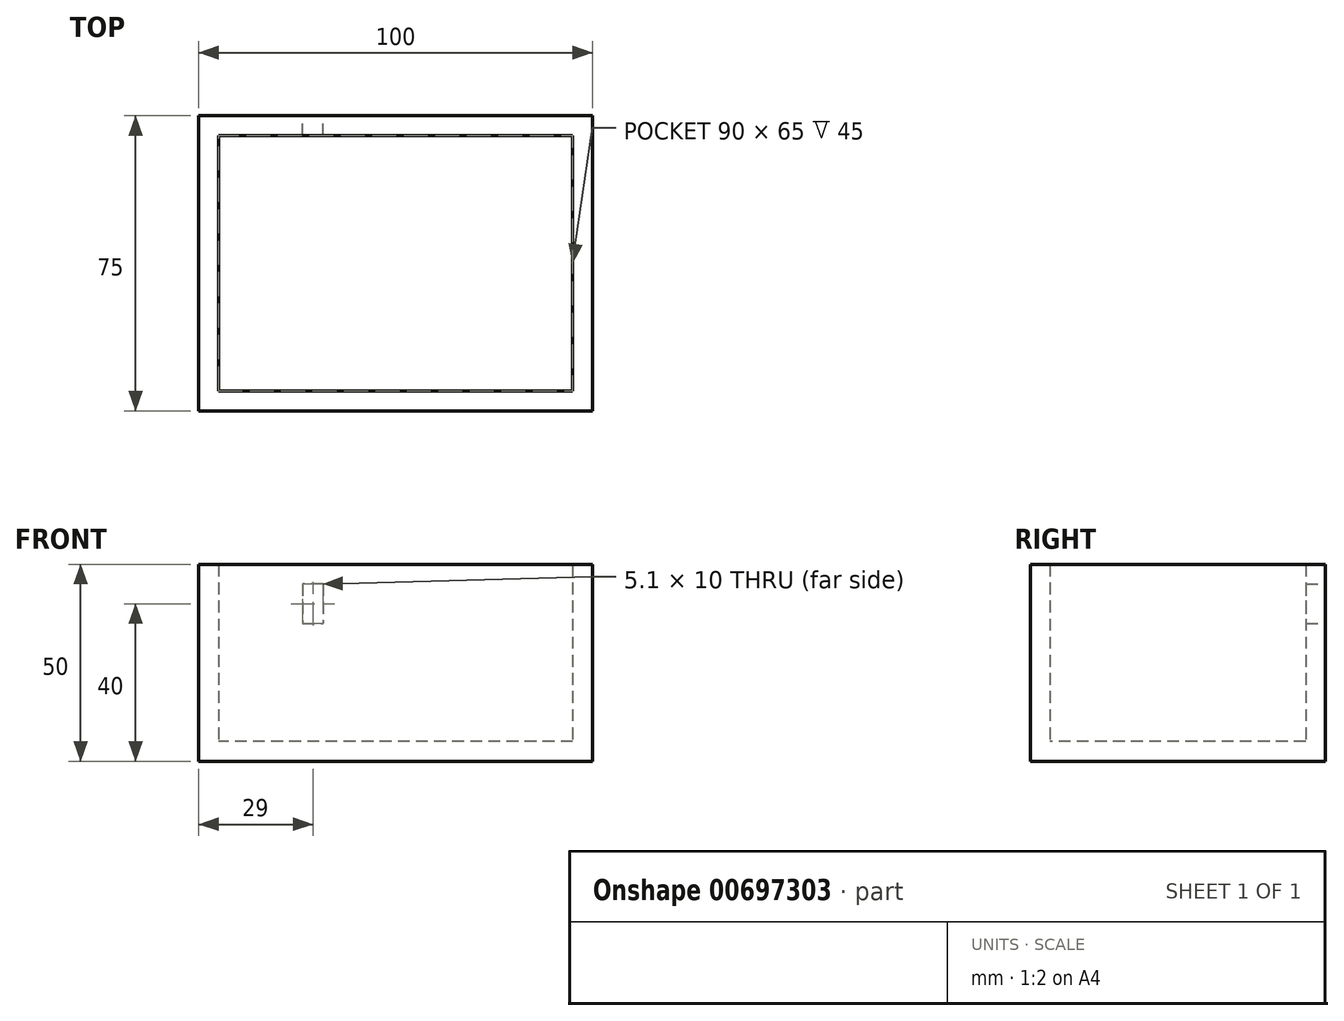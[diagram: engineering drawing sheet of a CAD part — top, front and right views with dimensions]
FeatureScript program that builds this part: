
annotation { "Feature Type Name" : "Feature", "Feature Type Description" : "" }
export const myFeature = defineFeature(function(context is Context, id is Id, definition is map)
    precondition{}
    {
        {
            var Q0;
            Q0=qCreatedBy(makeId("Top.planeOp"),FACE);
            var sketch = newSketch(context, id + "F0", { "sketchPlane" : qUnion([Q0])});
            skLineSegment(sketch, "E0.bottom", {"start": v(-48.95, 46.06) * mm, "end": v(51.05, 46.06) * mm});
            skLineSegment(sketch, "E0.top", {"start": v(-48.95, -28.94) * mm, "end": v(51.05, -28.94) * mm});
            skLineSegment(sketch, "E0.left", {"start": v(-48.95, 46.06) * mm, "end": v(-48.95, -28.94) * mm});
            skLineSegment(sketch, "E0.right", {"start": v(51.05, 46.06) * mm, "end": v(51.05, -28.94) * mm});
            skSolve(sketch);
        }
        {
            var Q0;
            Q0=makeQuery(id+"F0.imprint","IMPRINT",FACE,{"disambiguationData":[TD([[makeQuery(id+"F0.imprint","IMPRINT",EDGE,{"derivedFrom":sQuery(id+"F0.wireOp",EDGE,"E0.bottom")}),-1.0]])]});
            var sketch = newSketch(context, id + "F1", { "sketchPlane" : qUnion([Q0])});
            skLineSegment(sketch, "E1.bottom", {"start": v(-43.95, -23.94) * mm, "end": v(46.05, -23.94) * mm});
            skLineSegment(sketch, "E1.top", {"start": v(-43.95, 41.06) * mm, "end": v(46.05, 41.06) * mm});
            skLineSegment(sketch, "E1.left", {"start": v(-43.95, -23.94) * mm, "end": v(-43.95, 41.06) * mm});
            skLineSegment(sketch, "E1.right", {"start": v(46.05, -23.94) * mm, "end": v(46.05, 41.06) * mm});
            skSolve(sketch);
        }
        {
            var Q0;
            Q0=makeQuery(id+"F1.imprint","IMPRINT",FACE,{"disambiguationData":[TD([[makeQuery(id+"F1.imprint","IMPRINT",EDGE,{"derivedFrom":sQuery(id+"F1.wireOp",EDGE,"E1.bottom")}),1.0]])]});
            var Q1;
            Q1=makeQuery(id+"F1.imprint","IMPRINT",FACE,{"disambiguationData":[TD([[makeQuery(id+"F1.imprint","IMPRINT",EDGE,{"derivedFrom":sQuery(id+"F1.wireOp",EDGE,"E1.bottom")}),-1.0]])]});
            extrude(context, id + "F2", {"entities" : qUnion([Q0, Q1]), "depth" : 5 * mm, "offsetDistance" : 25 * mm});
        }
        {
            var Q0;
            Q0=makeQuery(id+"F1.imprint","IMPRINT",FACE,{"disambiguationData":[TD([[makeQuery(id+"F1.imprint","IMPRINT",EDGE,{"derivedFrom":sQuery(id+"F1.wireOp",EDGE,"E1.bottom")}),-1.0]])]});
            extrude(context, id + "F3", {"entities" : qUnion([Q0]), "operationType" : NewBodyOperationType.ADD, "depth" : 50 * mm, "offsetDistance" : 25 * mm});
        }
        {
            var Q0;
            {var subQ0=sQuery(id+"F0.wireOp",EDGE,"E0.bottom");Q0=makeQuery(id+"F3.boolean.opBoolean","MERGE",FACE,{"derivedFrom":[makeQuery(id+"F2.opExtrude","SWEPT_FACE",FACE,{"disambiguationData":[OSD([subQ0])]}),makeQuery(id+"F3.opExtrude","SWEPT_FACE",FACE,{"disambiguationData":[OSD([subQ0])]})]});}
            var sketch = newSketch(context, id + "F4", { "sketchPlane" : qUnion([Q0])});
            skLineSegment(sketch, "E2", {"start": v(-22.5, 45) * mm, "end": v(22.5, 45) * mm});
            skLineSegment(sketch, "E3.top", {"start": v(-17.5, 40) * mm, "end": v(-2.5, 40) * mm});
            skLineSegment(sketch, "E3.left", {"start": v(-22.5, 45) * mm, "end": v(-22.5, 40) * mm});
            skPoint(sketch, "E4.endSnap0", {"position": v(0, 45) * mm});
            skLineSegment(sketch, "E5.bottom", {"start": v(-22.5, 45) * mm, "end": v(-17.4, 45) * mm});
            skLineSegment(sketch, "E5.top", {"start": v(-22.5, 35) * mm, "end": v(-17.4, 35) * mm});
            skLineSegment(sketch, "E5.left", {"start": v(-22.5, 45) * mm, "end": v(-22.5, 35) * mm});
            skLineSegment(sketch, "E5.right", {"start": v(-17.4, 45) * mm, "end": v(-17.4, 35) * mm});
            skLineSegment(sketch, "E6.MirrorCS", {"start": v(22.5, 35) * mm, "end": v(17.4, 35) * mm});
            skLineSegment(sketch, "E7.MirrorCS", {"start": v(17.4, 45) * mm, "end": v(17.4, 35) * mm});
            skLineSegment(sketch, "E8.bottom", {"start": v(-2.55, 45) * mm, "end": v(2.55, 45) * mm});
            skLineSegment(sketch, "E8.top", {"start": v(-2.55, 35) * mm, "end": v(2.55, 35) * mm});
            skLineSegment(sketch, "E8.left", {"start": v(-2.55, 45) * mm, "end": v(-2.55, 35) * mm});
            skLineSegment(sketch, "E8.right", {"start": v(2.55, 45) * mm, "end": v(2.55, 35) * mm});
            skPoint(sketch, "E9.MirrorCS.end.orphan", {"position": v(2.5, 40) * mm});
            skPoint(sketch, "E9.MirrorCS.start.orphan", {"position": v(2.5, 45) * mm});
            skPoint(sketch, "E10.end.orphan", {"position": v(-2.5, 40) * mm});
            skPoint(sketch, "E10.start.orphan", {"position": v(-2.5, 45) * mm});
            skLineSegment(sketch, "E11.trimOffspring", {"start": v(2.5, 40) * mm, "end": v(17.4, 40) * mm});
            skPoint(sketch, "E4.end.orphan", {"position": v(17.5, 45) * mm});
            skLineSegment(sketch, "E12", {"start": v(22.5, 45) * mm, "end": v(22.5, 35) * mm});
            skSolve(sketch);
        }
        {
            var Q0;
            {var subQ3=sQuery(id+"F4.wireOp",EDGE,"E5.bottom");Q0=makeQuery(id+"F4.imprint","IMPRINT",FACE,{"disambiguationData":[TD([[makeQuery(id+"F4.imprint","IMPRINT",EDGE,{"derivedFrom":subQ3}),-1.0]])]});}
            var Q1;
            {var subQ3=sQuery(id+"F4.wireOp",EDGE,"E8.bottom");Q1=makeQuery(id+"F4.imprint","IMPRINT",FACE,{"disambiguationData":[TD([[makeQuery(id+"F4.imprint","IMPRINT",EDGE,{"derivedFrom":subQ3}),-1.0]])]});}
            var Q2;
            {var subQ4=sQuery(id+"F4.wireOp",EDGE,"E6.MirrorCS");Q2=makeQuery(id+"F4.imprint","IMPRINT",FACE,{"disambiguationData":[TD([[makeQuery(id+"F4.imprint","IMPRINT",EDGE,{"derivedFrom":subQ4}),-1.0]])]});}
            extrude(context, id + "F5", {"entities" : qUnion([Q0, Q1, Q2]), "operationType" : NewBodyOperationType.REMOVE, "oppositeDirection" : true, "depth" : 5 * mm, "offsetDistance" : 25 * mm});
        }
    });
